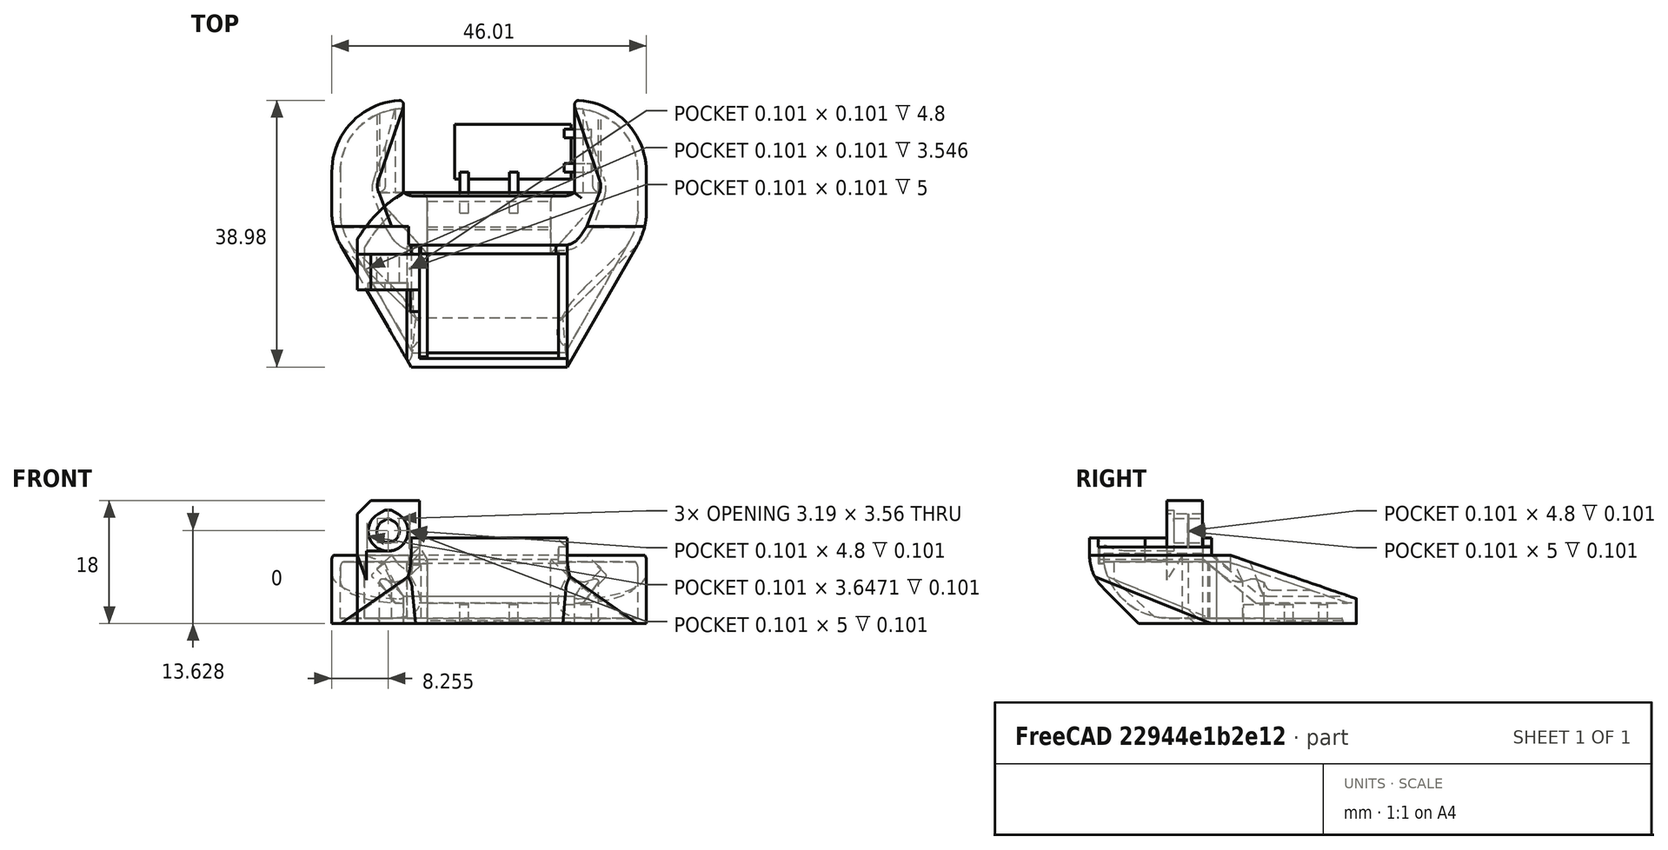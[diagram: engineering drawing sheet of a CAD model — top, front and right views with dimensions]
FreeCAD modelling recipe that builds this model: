
FCSTD DOCUMENT  (FreeCAD 0.18R14555 (Git shallow))
Label: duct
License: All rights reserved
LicenseURL: http://en.wikipedia.org/wiki/All_rights_reserved
objects: Part::Box×14, Part::MultiFuse×6, Part::Cut×4, Part::Chamfer×4, Part::Feature×3, Part::Cylinder×3, Part::MultiCommon×1
note: 35 computed .brp shape members not serialized (recipe doc carries the construction recipe); baked Part::Feature solids carry a one-line shape summary decoded from their .brp

FEATURE [Part::Feature] Part__Feature050  label="nozzle_fan_duct"
  Placement = pos=(0.005,14,-6.0794e-11) rot=(0,0,1;0rad)
  shape: bbox 46.01 x 38.99 x 18.01 mm, 128 faces (baked)
FEATURE [Part::Feature] Part__Feature050001  label="origin"
  shape: bbox 46.01 x 38.99 x 18.01 mm, 128 faces (baked)
FEATURE [Part::Cylinder] Cylinder  label="outer"
  Angle = 360
  AttacherType = Attacher::AttachEngine3D
  Height = 9
  Placement = pos=(-2,-17,0) rot=(0,0,1;0rad)
  Radius = 20
FEATURE [Part::Cylinder] Cylinder001  label="inner"
  Angle = 360
  AttacherType = Attacher::AttachEngine3D
  Height = 9
  Placement = pos=(-2,-17,0) rot=(0,0,1;0rad)
  Radius = 18.5
FEATURE [Part::Cylinder] Cylinder002  label="outer001"
  Angle = 360
  AttacherType = Attacher::AttachEngine3D
  Height = 22
  Placement = pos=(-2,-17,0) rot=(0,0,1;0rad)
  Radius = 20
FEATURE [Part::Cut] Cut
  Base = -> Cylinder
  Tool = -> Cylinder001
FEATURE [Part::Box] Box  label="Cube"
  AttacherType = Attacher::AttachEngine3D
  Height = 22
  Length = 38
  Placement = pos=(-11,-18,0) rot=(0,0,1;0rad)
  Width = 40
FEATURE [Part::MultiFuse] Fusion
  Shapes = -> [Box,Cylinder002]
FEATURE [Part::Box] Box001  label="Cube001"
  AttacherType = Attacher::AttachEngine3D
  Height = 16
  Length = 10
  Placement = pos=(-12.2555,-4.63713,0) rot=(0,0,1;0.698132rad)
  Width = 10
FEATURE [Part::Box] Box002  label="Cube002"
  AttacherType = Attacher::AttachEngine3D
  Height = 10
  Length = 10
  Placement = pos=(-29,-19,0) rot=(0,0,1;0rad)
  Width = 10
FEATURE [Part::Box] Box003  label="Cube003"
  AttacherType = Attacher::AttachEngine3D
  Height = 10
  Length = 32
  Placement = pos=(-10,-38,0) rot=(0,0,1;0rad)
  Width = 43
FEATURE [Part::Box] Box004  label="Cube004"
  AttacherType = Attacher::AttachEngine3D
  Height = 10
  Length = 20
  Placement = pos=(-29,-38,0) rot=(0,0,1;0rad)
  Width = 20
FEATURE [Part::MultiCommon] Common
  Shapes = -> [Fusion,Part__Feature050001]
FEATURE [Part::MultiFuse] Fusion001
  Shapes = -> [Box001,Box004,Box003,Box002]
FEATURE [Part::Cut] Cut001
  Base = -> Cut
  Tool = -> Fusion001
FEATURE [Part::Chamfer] Chamfer
  Base = -> Cut001
  Edges = 1 edges: [Edge5 r1=1 r2=1.5]
FEATURE [Part::Box] Box005  label="Cube005"
  AttacherType = Attacher::AttachEngine3D
  Height = 11.2
  Length = 3
  Placement = pos=(-11.99,-24,0) rot=(0,0,1;0rad)
  Width = 16.1
FEATURE [Part::Chamfer] Chamfer002
  Base = -> Box005
  Edges = 1 edges: [Edge6 r1=1.79 r2=1.16]
FEATURE [Part::Box] Box006  label="Cube006"
  AttacherType = Attacher::AttachEngine3D
  Height = 10
  Length = 10
  Placement = pos=(-20.15,-9.2,9.995) rot=(0,0,1;0rad)
  Width = 10
FEATURE [Part::Box] Box007  label="Cube007"
  AttacherType = Attacher::AttachEngine3D
  Height = 10
  Length = 1
  Placement = pos=(-19.25,-11.88,0) rot=(0,0,1;0rad)
  Width = 4
FEATURE [Part::Box] Box008  label="Cube008"
  AttacherType = Attacher::AttachEngine3D
  Height = 14
  Length = 10
  Placement = pos=(-29.25,-15,0) rot=(0,0,1;0rad)
  Width = 10
FEATURE [Part::Chamfer] Chamfer004
  Base = -> Box007
  Edges = 1 edges r=2.1: [Edge9]
FEATURE [Part::Box] Box009  label="Cube009"
  AttacherType = Attacher::AttachEngine3D
  Height = 2.8
  Length = 1.25
  Placement = pos=(3,-3,0) rot=(0,0,1;0rad)
  Width = 6
FEATURE [Part::Box] Box010  label="Cube010"
  AttacherType = Attacher::AttachEngine3D
  Height = 2.8
  Length = 1.25
  Placement = pos=(-4.25,-3,0) rot=(0,0,1;0rad)
  Width = 6
FEATURE [Part::Box] Box011  label="Cube011"
  AttacherType = Attacher::AttachEngine3D
  Height = 2.8
  Length = 4
  Placement = pos=(11,3,0) rot=(0,0,1;0rad)
  Width = 1.25
FEATURE [Part::Box] Box012  label="Cube012"
  AttacherType = Attacher::AttachEngine3D
  Height = 2.8
  Length = 4
  Placement = pos=(11,8,0) rot=(0,0,1;0rad)
  Width = 1.25
FEATURE [Part::Box] Box013  label="Cube013"
  AttacherType = Attacher::AttachEngine3D
  Height = 0.2
  Length = 17
  Placement = pos=(-5,2,0) rot=(0,0,1;0rad)
  Width = 8
FEATURE [Part::MultiFuse] Fusion003002  label="custom-support"
  Shapes = -> [Box013,Box012,Box009,Box011,Box010]
FEATURE [Part::Cut] Cut002
  Base = -> Chamfer002
  Tool = -> Box006
FEATURE [Part::Chamfer] Chamfer005
  Base = -> Cut002
  Edges = 1 edges: [Edge6 r1=6.5 r2=7]
FEATURE [Part::MultiFuse] Fusion003003
  Shapes = -> [Chamfer005,Common]
FEATURE [Part::MultiFuse] Fusion003004
  Shapes = -> [Fusion003003,Chamfer]
FEATURE [Part::Cut] Cut003
  Base = -> Fusion003004
  Tool = -> Box008
FEATURE [Part::MultiFuse] Fusion003005  label="rev1-origin"
  Shapes = -> [Chamfer004,Cut003]
FEATURE [Part::Feature] Fusion003005001  label="rev1-origin001"
  shape: bbox 42.27 x 38.99 x 18.01 mm, 132 faces (baked)
